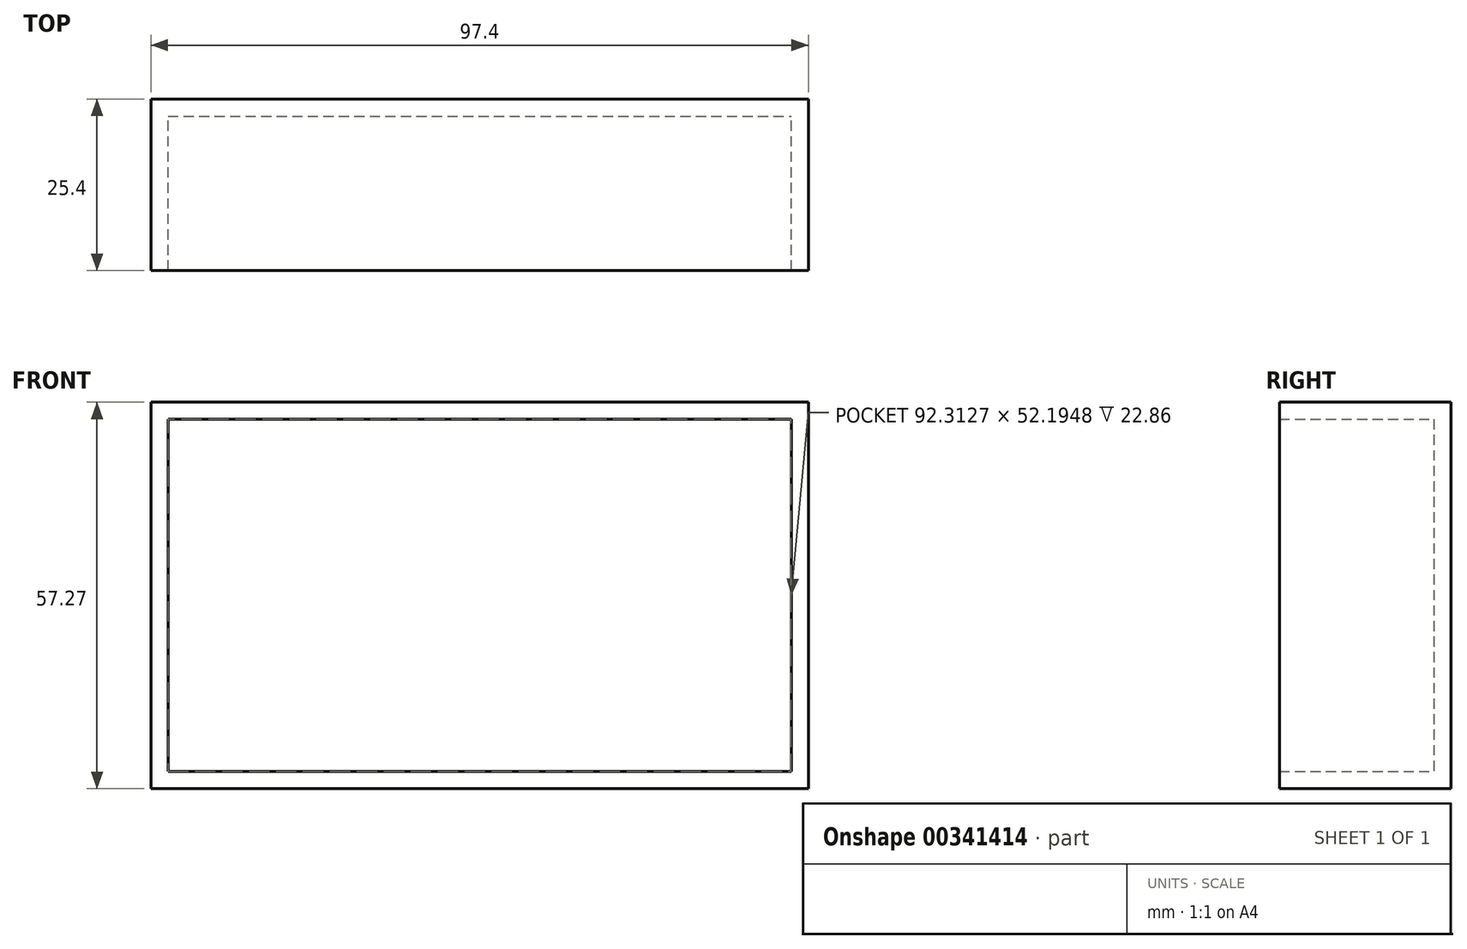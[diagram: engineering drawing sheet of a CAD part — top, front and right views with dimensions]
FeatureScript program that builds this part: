
annotation { "Feature Type Name" : "Feature", "Feature Type Description" : "" }
export const myFeature = defineFeature(function(context is Context, id is Id, definition is map)
    precondition{}
    {
        {
            var Q0;
            Q0=qCreatedBy(makeId("Front.planeOp"),FACE);
            var sketch = newSketch(context, id + "F0", { "sketchPlane" : qUnion([Q0])});
            skLineSegment(sketch, "E0.bottom", {"start": v(-41.32, 18.38) * mm, "end": v(56.08, 18.38) * mm});
            skLineSegment(sketch, "E0.top", {"start": v(-41.32, -38.9) * mm, "end": v(56.08, -38.9) * mm});
            skLineSegment(sketch, "E0.left", {"start": v(-41.32, 18.38) * mm, "end": v(-41.32, -38.9) * mm});
            skLineSegment(sketch, "E0.right", {"start": v(56.08, 18.38) * mm, "end": v(56.08, -38.9) * mm});
            skSolve(sketch);
        }
        {
            var Q0;
            Q0=qSketchRegion(id+"F0",true);
            extrude(context, id + "F1", {"entities" : qUnion([Q0]), "depth" : 25.4 * mm});
        }
        {
            var Q0;
            Q0=makeQuery(id+"F1.opExtrude","CAP_FACE",FACE,{"disambiguationData":[OSD([sQuery(id+"F0.wireOp",EDGE,"E0.bottom"),sQuery(id+"F0.wireOp",EDGE,"E0.top"),sQuery(id+"F0.wireOp",EDGE,"E0.left"),sQuery(id+"F0.wireOp",EDGE,"E0.right")])],"isStart":false});
            shell(context, id + "F2", {"entities" : qUnion([Q0]), "thickness" : 2.54 * mm});
        }
        {
            var Q0;
            Q0=qCreatedBy(makeId("Right.planeOp"),FACE);
            var sketch = newSketch(context, id + "F3", { "sketchPlane" : qUnion([Q0])});
            skLineSegment(sketch, "E1", {"start": v(95.57, -11.33) * mm, "end": v(138.49, -92.85) * mm});
            skLineSegment(sketch, "E2", {"start": v(138.49, -92.85) * mm, "end": v(89.32, -150.45) * mm});
            skLineSegment(sketch, "E3", {"start": v(89.32, -150.45) * mm, "end": v(27.85, -140.06) * mm});
            skLineSegment(sketch, "E4", {"start": v(27.85, -140.06) * mm, "end": v(17.22, -58.95) * mm});
            skLineSegment(sketch, "E5", {"start": v(17.22, -58.95) * mm, "end": v(51.6, 2.23) * mm});
            skLineSegment(sketch, "E6", {"start": v(51.6, 2.23) * mm, "end": v(91.82, 8) * mm});
            skLineSegment(sketch, "E7", {"start": v(91.82, 8) * mm, "end": v(99.1, -8.85) * mm});
            skSolve(sketch);
        }
        {
            var Q0;
            Q0 = qSketchRegion(id + "F3", true);
            var Q1;
            Q1=sQuery(id+"F3.wireOp",EDGE,"E1");
            var Q2;
            Q2=sQuery(id+"F3.wireOp",EDGE,"E2");
            var Q3;
            Q3=sQuery(id+"F3.wireOp",EDGE,"E3");
            extrude(context, id + "F4", {"entities" : qUnion([Q0]), "bodyType" : ToolBodyType.SURFACE, "surfaceEntities" : qUnion([Q1, Q2, Q3]), "depth" : 119.27 * mm});
        }
    });
